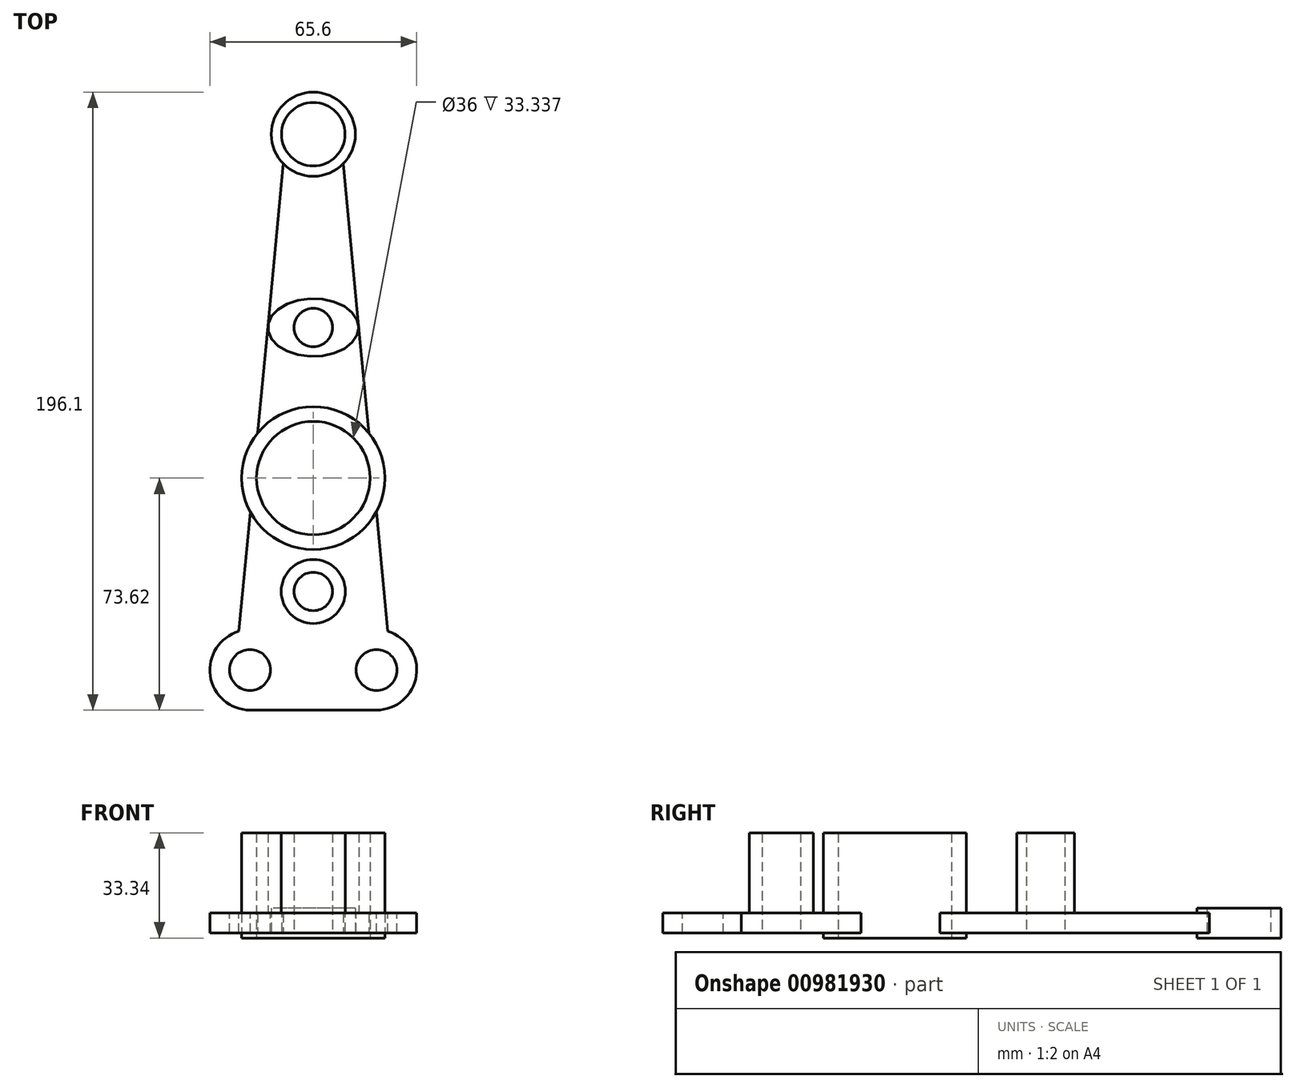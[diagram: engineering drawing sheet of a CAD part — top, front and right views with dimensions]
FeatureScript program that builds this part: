
annotation { "Feature Type Name" : "Feature", "Feature Type Description" : "" }
export const myFeature = defineFeature(function(context is Context, id is Id, definition is map)
    precondition{}
    {
        {
            var Q0;
            Q0=qCreatedBy(makeId("Top.planeOp"),FACE);
            var sketch = newSketch(context, id + "F0", { "sketchPlane" : qUnion([Q0])});
            skCircle(sketch, "E0", {"center": v(0, 0) * mm, "radius": 18 * mm});
            skCircle(sketch, "E1", {"center": v(0, 0) * mm, "radius": 22.7 * mm});
            skCircle(sketch, "E2", {"center": v(0, -35.97) * mm, "radius": 6.1 * mm});
            skCircle(sketch, "E3", {"center": v(0, -35.97) * mm, "radius": 10.16 * mm});
            skCircle(sketch, "E4", {"center": v(0, 47.79) * mm, "radius": 6.07 * mm});
            skCircle(sketch, "E5", {"center": v(0, 109.13) * mm, "radius": 10.08 * mm});
            skCircle(sketch, "E6", {"center": v(0, 109.13) * mm, "radius": 13.35 * mm});
            skEllipse(sketch, "E7", {"center": v(0, 47.79) * mm, "majorRadius": 14.42 * mm, "minorRadius": 9.82 * mm, "majorAxis": v(1, 0)});
            skLineSegment(sketch, "E8", {"start": v(0, 109.13) * mm, "end": v(0, 0) * mm, "construction": true});
            skPoint(sketch, "E9.endSnap0", {"position": v(14.42, 47.79) * mm});
            skLineSegment(sketch, "E10", {"start": v(9.52, 99.78) * mm, "end": v(17.63, 14.3) * mm});
            skLineSegment(sketch, "E11.MirrorCS", {"start": v(-9.52, 99.78) * mm, "end": v(-17.63, 14.3) * mm});
            skLineSegment(sketch, "E12", {"start": v(7.02, -21.58) * mm, "end": v(8.42, -30.27) * mm});
            skLineSegment(sketch, "E13.MirrorCS", {"start": v(-7.02, -21.58) * mm, "end": v(-8.42, -30.27) * mm});
            skSolve(sketch);
        }
        {
            var Q0;
            Q0=qSketchRegion(id+"F0",true);
            extrude(context, id + "F1", {"entities" : qUnion([Q0]), "depth" : 6.35 * mm, "offsetDistance" : 25.4 * mm});
        }
        {
            var Q0;
            Q0=makeQuery(id+"F1.opExtrude","CAP_FACE",FACE,{"disambiguationData":[OSD([sQuery(id+"F0.wireOp",EDGE,"E0"),sQuery(id+"F0.wireOp",EDGE,"E1"),sQuery(id+"F0.wireOp",EDGE,"E2"),sQuery(id+"F0.wireOp",EDGE,"E3"),sQuery(id+"F0.wireOp",EDGE,"E4"),sQuery(id+"F0.wireOp",EDGE,"E5"),sQuery(id+"F0.wireOp",EDGE,"E6"),sQuery(id+"F0.wireOp",EDGE,"E10"),sQuery(id+"F0.wireOp",EDGE,"E11.MirrorCS"),sQuery(id+"F0.wireOp",EDGE,"E12"),sQuery(id+"F0.wireOp",EDGE,"E13.MirrorCS")])],"isStart":false});
            var sketch = newSketch(context, id + "F2", { "sketchPlane" : qUnion([Q0])});
            skCircle(sketch, "E14", {"center": v(0, 0) * mm, "radius": 18 * mm});
            skCircle(sketch, "E15", {"center": v(0, 0) * mm, "radius": 22.7 * mm});
            skCircle(sketch, "E16", {"center": v(0, -35.97) * mm, "radius": 6.1 * mm});
            skCircle(sketch, "E17", {"center": v(0, -35.97) * mm, "radius": 10.16 * mm});
            skCircle(sketch, "E18", {"center": v(0, 47.79) * mm, "radius": 6.07 * mm});
            skCircle(sketch, "E19", {"center": v(0, 109.13) * mm, "radius": 10.08 * mm});
            skCircle(sketch, "E20", {"center": v(0, 109.13) * mm, "radius": 13.35 * mm});
            skEllipse(sketch, "E21", {"center": v(0, 47.79) * mm, "majorRadius": 14.42 * mm, "minorRadius": 9.15 * mm, "majorAxis": v(1, 0)});
            skLineSegment(sketch, "E22", {"start": v(0, 109.13) * mm, "end": v(0, 0) * mm, "construction": true});
            skPoint(sketch, "E23.endSnap0", {"position": v(14.42, 47.79) * mm});
            skLineSegment(sketch, "E24", {"start": v(9.52, 99.78) * mm, "end": v(17.63, 14.3) * mm});
            skLineSegment(sketch, "E25.MirrorCS", {"start": v(-9.52, 99.78) * mm, "end": v(-17.63, 14.3) * mm});
            skLineSegment(sketch, "E26", {"start": v(7.02, -21.58) * mm, "end": v(8.42, -30.27) * mm});
            skLineSegment(sketch, "E27.MirrorCS", {"start": v(-7.02, -21.58) * mm, "end": v(-8.42, -30.27) * mm});
            skSolve(sketch);
        }
        {
            var Q0;
            Q0=makeQuery(id+"F2.imprint","IMPRINT",FACE,{"disambiguationData":[TD([[makeQuery(id+"F2.imprint","IMPRINT",EDGE,{"derivedFrom":sQuery(id+"F2.wireOp",EDGE,"E16")}),-1.0]])]});
            var Q1;
            Q1=makeQuery(id+"F2.imprint","IMPRINT",FACE,{"disambiguationData":[TD([[makeQuery(id+"F2.imprint","IMPRINT",EDGE,{"derivedFrom":sQuery(id+"F2.wireOp",EDGE,"E19")}),-1.0]])]});
            var Q2;
            Q2=makeQuery(id+"F2.imprint","IMPRINT",FACE,{"disambiguationData":[TD([[makeQuery(id+"F2.imprint","IMPRINT",EDGE,{"derivedFrom":sQuery(id+"F2.wireOp",EDGE,"E14")}),-1.0]])]});
            var Q3;
            Q3=makeQuery(id+"F2.imprint","IMPRINT",FACE,{"disambiguationData":[TD([[makeQuery(id+"F2.imprint","IMPRINT",EDGE,{"derivedFrom":sQuery(id+"F2.wireOp",EDGE,"E18")}),-1.0]])]});
            extrude(context, id + "F3", {"entities" : qUnion([Q0, Q1, Q2, Q3]), "operationType" : NewBodyOperationType.ADD, "depth" : 25.4 * mm, "offsetDistance" : 25.4 * mm});
        }
        {
            var Q0;
            Q0=makeQuery(id+"F3.opExtrude","CAP_FACE",FACE,{"disambiguationData":[OSD([sQuery(id+"F2.wireOp",EDGE,"E14"),sQuery(id+"F2.wireOp",EDGE,"E15")])],"isStart":false});
            var sketch = newSketch(context, id + "F4", { "sketchPlane" : qUnion([Q0])});
            skSolve(sketch);
        }
        {
            var Q0;
            Q0 = qSketchRegion(id + "F4", true);
            var Q1;
            Q1=makeQuery(id+"F4.imprint","IMPRINT",FACE,{"disambiguationData":[TD([[makeQuery(id+"F4.imprint","IMPRINT",EDGE,{"derivedFrom":makeQuery(id+"F3.opExtrude","CAP_EDGE",EDGE,{"disambiguationData":[OSD([sQuery(id+"F2.wireOp",EDGE,"E14")])],"isStart":false})}),-1.0]])]});
            var Q2;
            Q2=makeQuery(id+"F3.opExtrude","CAP_FACE",FACE,{"disambiguationData":[OSD([sQuery(id+"F2.wireOp",EDGE,"E19"),sQuery(id+"F2.wireOp",EDGE,"E20")])],"isStart":false});
            extrude(context, id + "F5", {"entities" : qUnion([Q0, Q1, Q2]), "operationType" : NewBodyOperationType.REMOVE, "oppositeDirection" : true, "depth" : 23.8 * mm, "offsetDistance" : 25.4 * mm});
        }
        {
            var Q0;
            Q0=makeQuery(id+"F1.opExtrude","CAP_FACE",FACE,{"disambiguationData":[OSD([sQuery(id+"F0.wireOp",EDGE,"E0"),sQuery(id+"F0.wireOp",EDGE,"E1"),sQuery(id+"F0.wireOp",EDGE,"E2"),sQuery(id+"F0.wireOp",EDGE,"E3"),sQuery(id+"F0.wireOp",EDGE,"E4"),sQuery(id+"F0.wireOp",EDGE,"E5"),sQuery(id+"F0.wireOp",EDGE,"E6"),sQuery(id+"F0.wireOp",EDGE,"E10"),sQuery(id+"F0.wireOp",EDGE,"E11.MirrorCS"),sQuery(id+"F0.wireOp",EDGE,"E12"),sQuery(id+"F0.wireOp",EDGE,"E13.MirrorCS")])],"isStart":true});
            var sketch = newSketch(context, id + "F6", { "sketchPlane" : qUnion([Q0])});
            skCircle(sketch, "E28", {"center": v(0, -109.13) * mm, "radius": 13.35 * mm});
            skCircle(sketch, "E29", {"center": v(0, 0) * mm, "radius": 22.7 * mm});
            skCircle(sketch, "E30.0", {"center": v(0, 0) * mm, "radius": 18 * mm});
            skCircle(sketch, "E31.0", {"center": v(0, -109.13) * mm, "radius": 10.08 * mm});
            skSolve(sketch);
        }
        {
            var Q0;
            Q0 = qSketchRegion(id + "F6", true);
            extrude(context, id + "F7", {"entities" : qUnion([Q0]), "operationType" : NewBodyOperationType.ADD, "depth" : 1.59 * mm, "offsetDistance" : 25.4 * mm});
        }
        {
            var Q0;
            {var subQ0=sQuery(id+"F0.wireOp",EDGE,"E12");var subQ1=sQuery(id+"F0.wireOp",EDGE,"E3");var subQ2=sQuery(id+"F0.wireOp",EDGE,"E10");var subQ3=sQuery(id+"F0.wireOp",EDGE,"E1");var subQ4=sQuery(id+"F0.wireOp",EDGE,"E11.MirrorCS");var subQ5=sQuery(id+"F0.wireOp",EDGE,"E13.MirrorCS");Q0=makeQuery(id+"F3.boolean.opBoolean","SPLIT",FACE,{"disambiguationData":[TD([makeQuery(id+"F1.opExtrude","SWEPT_FACE",FACE,{"disambiguationData":[OSD([subQ3]),TDD([makeQuery(id+"F0.imprint","IMPRINT",EDGE,{"disambiguationData":[TD([[makeQuery(id+"F0.imprint","INTERSECT",VERTEX,{"derivedFrom":[subQ3,subQ4]}),-1.0]])],"derivedFrom":subQ3})])]}),makeQuery(id+"F1.opExtrude","SWEPT_FACE",FACE,{"disambiguationData":[OSD([subQ3]),TDD([makeQuery(id+"F0.imprint","IMPRINT",EDGE,{"disambiguationData":[TD([[makeQuery(id+"F0.imprint","INTERSECT",VERTEX,{"derivedFrom":[subQ3,subQ2]}),1.0]])],"derivedFrom":subQ3})])]}),makeQuery(id+"F1.opExtrude","SWEPT_FACE",FACE,{"disambiguationData":[OSD([subQ1])]}),makeQuery(id+"F1.opExtrude","SWEPT_FACE",FACE,{"disambiguationData":[OSD([subQ0])]}),makeQuery(id+"F1.opExtrude","SWEPT_FACE",FACE,{"disambiguationData":[OSD([subQ5])]}),makeQuery(id+"F3.opExtrude","SWEPT_FACE",FACE,{"disambiguationData":[OSD([sQuery(id+"F2.wireOp",EDGE,"E15")])]}),makeQuery(id+"F3.opExtrude","SWEPT_FACE",FACE,{"disambiguationData":[OSD([sQuery(id+"F2.wireOp",EDGE,"E17")])]})])],"derivedFrom":makeQuery(id+"F1.opExtrude","CAP_FACE",FACE,{"disambiguationData":[OSD([sQuery(id+"F0.wireOp",EDGE,"E0"),subQ3,sQuery(id+"F0.wireOp",EDGE,"E2"),subQ1,sQuery(id+"F0.wireOp",EDGE,"E4"),sQuery(id+"F0.wireOp",EDGE,"E5"),sQuery(id+"F0.wireOp",EDGE,"E6"),subQ2,subQ4,subQ0,subQ5])],"isStart":false})});}
            var sketch = newSketch(context, id + "F8", { "sketchPlane" : qUnion([Q0])});
            skCircle(sketch, "E32", {"center": v(-20.08, -60.9) * mm, "radius": 6.49 * mm});
            skCircle(sketch, "E33.MirrorC", {"center": v(20.08, -60.9) * mm, "radius": 6.49 * mm});
            skCircle(sketch, "E34", {"center": v(-20.08, -60.9) * mm, "radius": 12.73 * mm});
            skCircle(sketch, "E35.MirrorC", {"center": v(20.08, -60.9) * mm, "radius": 12.73 * mm});
            skLineSegment(sketch, "E36", {"start": v(-20.08, -73.62) * mm, "end": v(20.08, -73.62) * mm});
            skLineSegment(sketch, "E37.0", {"start": v(-20, -10.73) * mm, "end": v(-23.6, -48.66) * mm});
            skLineSegment(sketch, "E38.0", {"start": v(20, -10.73) * mm, "end": v(23.6, -48.66) * mm});
            skArc(sketch, "E39.0", {"start": v(-20, -10.73) * mm, "mid": v(0, -22.7) * mm, "end": v(20, -10.73) * mm});
            skCircle(sketch, "E40.0", {"center": v(0, -35.97) * mm, "radius": 6.1 * mm});
            skSolve(sketch);
        }
        {
            var Q0;
            Q0 = qSketchRegion(id + "F8", true);
            extrude(context, id + "F9", {"entities" : qUnion([Q0]), "operationType" : NewBodyOperationType.ADD, "oppositeDirection" : true, "depth" : 6.35 * mm, "offsetDistance" : 25.4 * mm});
        }
    });
